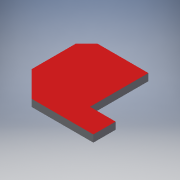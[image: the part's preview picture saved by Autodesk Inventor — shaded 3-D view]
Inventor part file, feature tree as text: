
AUTODESK INVENTOR PART (.ipt)
format: ipt  version: 2018 (Build 220112000, 112)  size: 125,440 bytes
history: native  units: mm
features: sketch x2, other x1, extrude x1, chamfer x1, hole x1
ambient origin geometry x8: Origin, YZ Plane, XZ Plane, XY Plane, X Axis, Y Axis, Z Axis, Center Point
bodies: Body1 (feature_tree)
feature tree (6):
  other  "Sólido1"
  extrude  "Extrusão1"  Depth=40.0mm
  chamfer  "Chanfro1"  Angle=135.0deg  [1 undecoded]
  hole  "Furo1"  [1 undecoded]
  sketch  "Esboço1"  dims[d0=111.0mm d5=40.0mm]
  sketch  "Esboço2"  dims[d6=105.0mm d7=135.0deg d8=98.71536mm d9=12.7mm d10=0.0mm d11=157.066236mm d12=20.0mm d13=2.0mm d14=45.0deg d15=4.134mm d16=10.0mm d17=4.0mm d18=2.0mm d19=90.0deg d20=14.2mm d21=20.594885mm]
note: 2 required parameter values undecoded (feature->parameter linkage not recoverable at this tier; creation-order binding heuristic only, values carry confidence <= 0.55)
